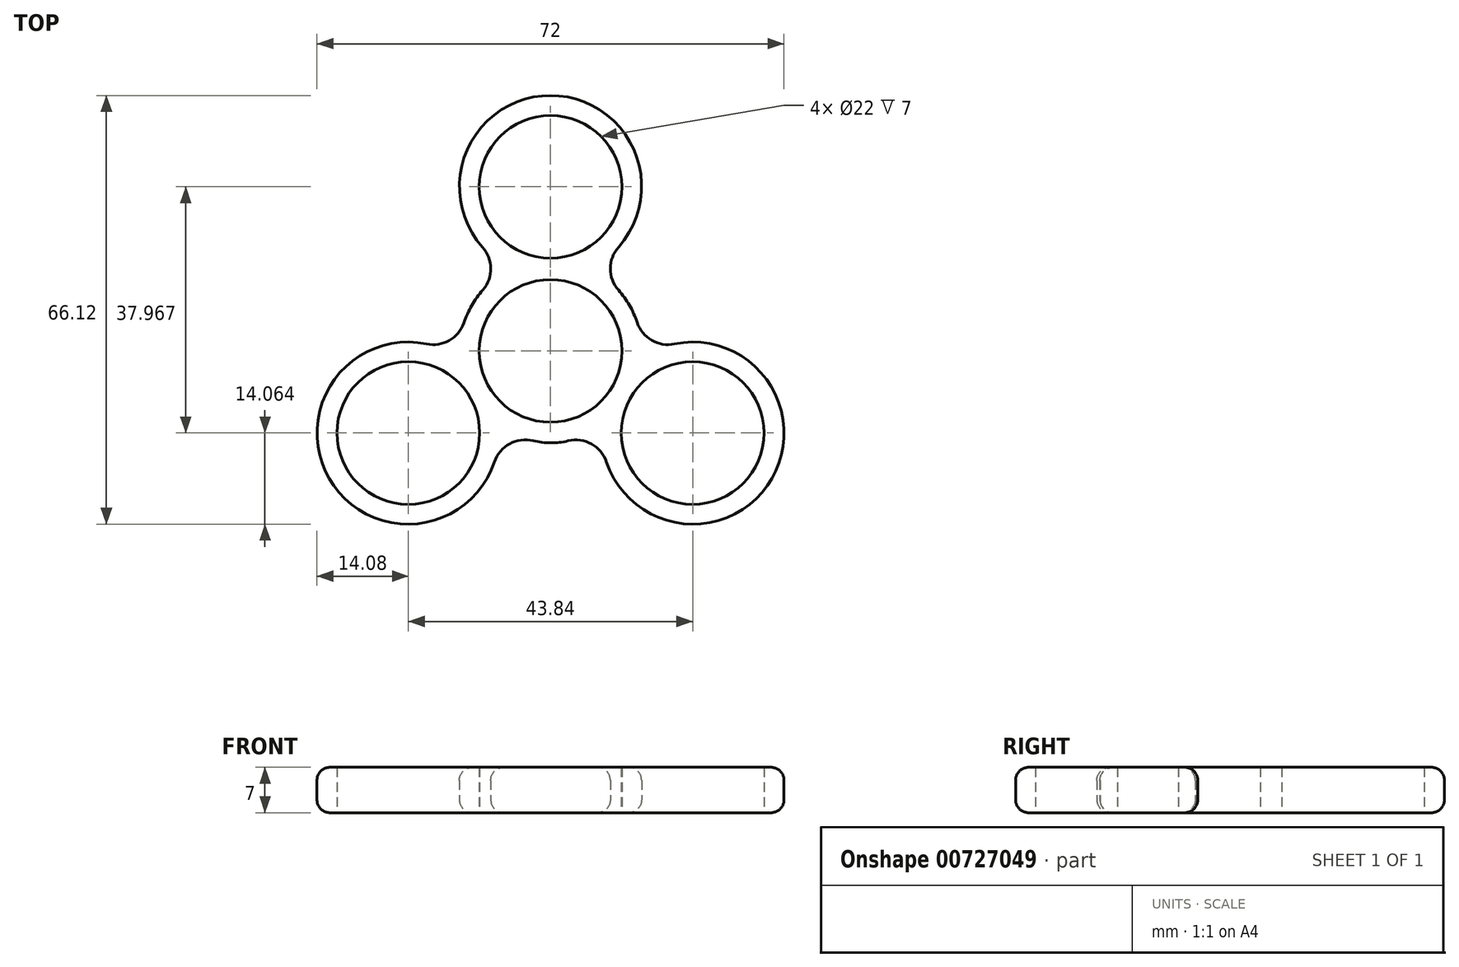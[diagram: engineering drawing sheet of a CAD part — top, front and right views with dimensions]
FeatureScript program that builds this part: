
annotation { "Feature Type Name" : "Feature", "Feature Type Description" : "" }
export const myFeature = defineFeature(function(context is Context, id is Id, definition is map)
    precondition{}
    {
        {
            var Q0;
            Q0=qCreatedBy(makeId("Top.planeOp"),FACE);
            var sketch = newSketch(context, id + "F0", { "sketchPlane" : qUnion([Q0])});
            skCircle(sketch, "E0", {"center": v(0, 0) * mm, "radius": 11 * mm});
            skCircle(sketch, "E1", {"center": v(0, 25.31) * mm, "radius": 11 * mm});
            skArc(sketch, "E2", {"start": v(10.49, 16.02) * mm, "mid": v(0, 39.4) * mm, "end": v(-10.48, 16.01) * mm});
            skArc(sketch, "E3.1.2", {"start": v(-19.1, 1.07) * mm, "mid": v(-34.13, -19.68) * mm, "end": v(-8.64, -17.12) * mm});
            skCircle(sketch, "E3.1.4", {"center": v(-21.92, -12.66) * mm, "radius": 11 * mm});
            skArc(sketch, "E3.2.2", {"start": v(8.64, -17.14) * mm, "mid": v(34.13, -19.68) * mm, "end": v(19.12, 1.07) * mm});
            skCircle(sketch, "E3.2.4", {"center": v(21.92, -12.66) * mm, "radius": 11 * mm});
            skArc(sketch, "E4", {"start": v(-10.42, 9.43) * mm, "mid": v(-12.13, 7.01) * mm, "end": v(-13.36, 4.33) * mm});
            skArc(sketch, "E5", {"start": v(13.36, 4.4) * mm, "mid": v(12.18, 7.03) * mm, "end": v(10.49, 9.37) * mm});
            skArc(sketch, "E6", {"start": v(-2.69, -13.85) * mm, "mid": v(0.02, -14.19) * mm, "end": v(2.72, -13.87) * mm});
            skPoint(sketch, "E7.newPointB", {"position": v(-8.44, -16.5) * mm});
            skArc(sketch, "E7.filletArc", {"start": v(-2.69, -13.85) * mm, "mid": v(-6.3, -14.32) * mm, "end": v(-8.64, -17.12) * mm});
            skPoint(sketch, "E8.newPointB", {"position": v(8.35, -16.14) * mm});
            skArc(sketch, "E8.filletArc", {"start": v(8.64, -17.14) * mm, "mid": v(6.32, -14.35) * mm, "end": v(2.72, -13.87) * mm});
            skPoint(sketch, "E9.newPointA", {"position": v(18.5, 0.93) * mm});
            skArc(sketch, "E9.filletArc", {"start": v(13.36, 4.4) * mm, "mid": v(15.6, 1.64) * mm, "end": v(19.12, 1.07) * mm});
            skPoint(sketch, "E10.newPointB", {"position": v(9.8, 15.3) * mm});
            skArc(sketch, "E10.filletArc", {"start": v(10.49, 16.02) * mm, "mid": v(9.22, 12.7) * mm, "end": v(10.49, 9.37) * mm});
            skPoint(sketch, "E11.newPointA", {"position": v(-10.06, 15.56) * mm});
            skArc(sketch, "E11.filletArc", {"start": v(-10.42, 9.43) * mm, "mid": v(-9.22, 12.73) * mm, "end": v(-10.48, 16.01) * mm});
            skPoint(sketch, "E12.newPointB", {"position": v(-18.15, 0.84) * mm});
            skArc(sketch, "E12.filletArc", {"start": v(-19.1, 1.07) * mm, "mid": v(-15.62, 1.62) * mm, "end": v(-13.36, 4.33) * mm});
            skSolve(sketch);
        }
        {
            var Q0;
            Q0 = qSketchRegion(id + "F0", true);
            extrude(context, id + "F1", {"entities" : qUnion([Q0]), "depth" : 7 * mm, "offsetDistance" : 25 * mm});
        }
        {
            var Q0;
            Q0=makeQuery(id+"F1.opExtrude","CAP_EDGE",EDGE,{"disambiguationData":[OSD([sQuery(id+"F0.wireOp",EDGE,"E4")])],"isStart":false});
            var Q1;
            Q1=makeQuery(id+"F1.opExtrude","CAP_EDGE",EDGE,{"disambiguationData":[OSD([sQuery(id+"F0.wireOp",EDGE,"E11.filletArc")])],"isStart":false});
            var Q2;
            Q2=makeQuery(id+"F1.opExtrude","CAP_EDGE",EDGE,{"disambiguationData":[OSD([sQuery(id+"F0.wireOp",EDGE,"E2")])],"isStart":false});
            var Q3;
            Q3=makeQuery(id+"F1.opExtrude","CAP_EDGE",EDGE,{"disambiguationData":[OSD([sQuery(id+"F0.wireOp",EDGE,"E5")])],"isStart":false});
            var Q4;
            Q4=makeQuery(id+"F1.opExtrude","CAP_EDGE",EDGE,{"disambiguationData":[OSD([sQuery(id+"F0.wireOp",EDGE,"E9.filletArc")])],"isStart":false});
            var Q5;
            Q5=makeQuery(id+"F1.opExtrude","CAP_EDGE",EDGE,{"disambiguationData":[OSD([sQuery(id+"F0.wireOp",EDGE,"E3.2.2")])],"isStart":false});
            var Q6;
            Q6=makeQuery(id+"F1.opExtrude","CAP_EDGE",EDGE,{"disambiguationData":[OSD([sQuery(id+"F0.wireOp",EDGE,"E8.filletArc")])],"isStart":false});
            var Q7;
            Q7=makeQuery(id+"F1.opExtrude","CAP_EDGE",EDGE,{"disambiguationData":[OSD([sQuery(id+"F0.wireOp",EDGE,"E6")])],"isStart":false});
            var Q8;
            Q8=makeQuery(id+"F1.opExtrude","CAP_EDGE",EDGE,{"disambiguationData":[OSD([sQuery(id+"F0.wireOp",EDGE,"E7.filletArc")])],"isStart":false});
            var Q9;
            Q9=makeQuery(id+"F1.opExtrude","CAP_EDGE",EDGE,{"disambiguationData":[OSD([sQuery(id+"F0.wireOp",EDGE,"E3.1.2")])],"isStart":false});
            var Q10;
            Q10=makeQuery(id+"F1.opExtrude","CAP_EDGE",EDGE,{"disambiguationData":[OSD([sQuery(id+"F0.wireOp",EDGE,"E12.filletArc")])],"isStart":false});
            var Q11;
            Q11=makeQuery(id+"F1.opExtrude","CAP_EDGE",EDGE,{"disambiguationData":[OSD([sQuery(id+"F0.wireOp",EDGE,"E5")])],"isStart":true});
            var Q12;
            Q12=makeQuery(id+"F1.opExtrude","CAP_EDGE",EDGE,{"disambiguationData":[OSD([sQuery(id+"F0.wireOp",EDGE,"E9.filletArc")])],"isStart":true});
            var Q13;
            Q13=makeQuery(id+"F1.opExtrude","CAP_EDGE",EDGE,{"disambiguationData":[OSD([sQuery(id+"F0.wireOp",EDGE,"E6")])],"isStart":true});
            var Q14;
            Q14=makeQuery(id+"F1.opExtrude","CAP_EDGE",EDGE,{"disambiguationData":[OSD([sQuery(id+"F0.wireOp",EDGE,"E8.filletArc")])],"isStart":true});
            var Q15;
            Q15=makeQuery(id+"F1.opExtrude","CAP_EDGE",EDGE,{"disambiguationData":[OSD([sQuery(id+"F0.wireOp",EDGE,"E7.filletArc")])],"isStart":true});
            var Q16;
            Q16=makeQuery(id+"F1.opExtrude","CAP_EDGE",EDGE,{"disambiguationData":[OSD([sQuery(id+"F0.wireOp",EDGE,"E3.1.2")])],"isStart":true});
            var Q17;
            Q17=makeQuery(id+"F1.opExtrude","CAP_EDGE",EDGE,{"disambiguationData":[OSD([sQuery(id+"F0.wireOp",EDGE,"E12.filletArc")])],"isStart":true});
            var Q18;
            Q18=makeQuery(id+"F1.opExtrude","CAP_EDGE",EDGE,{"disambiguationData":[OSD([sQuery(id+"F0.wireOp",EDGE,"E4")])],"isStart":true});
            var Q19;
            Q19=makeQuery(id+"F1.opExtrude","CAP_EDGE",EDGE,{"disambiguationData":[OSD([sQuery(id+"F0.wireOp",EDGE,"E11.filletArc")])],"isStart":true});
            var Q20;
            Q20=makeQuery(id+"F1.opExtrude","CAP_EDGE",EDGE,{"disambiguationData":[OSD([sQuery(id+"F0.wireOp",EDGE,"E2")])],"isStart":true});
            var Q21;
            Q21=makeQuery(id+"F1.opExtrude","CAP_EDGE",EDGE,{"disambiguationData":[OSD([sQuery(id+"F0.wireOp",EDGE,"E10.filletArc")])],"isStart":true});
            var Q22;
            Q22=makeQuery(id+"F1.opExtrude","CAP_EDGE",EDGE,{"disambiguationData":[OSD([sQuery(id+"F0.wireOp",EDGE,"E3.2.2")])],"isStart":true});
            fillet(context, id + "F2", {"entities" : qUnion([Q0, Q1, Q2, Q3, Q4, Q5, Q6, Q7, Q8, Q9, Q10, Q11, Q12, Q13, Q14, Q15, Q16, Q17, Q18, Q19, Q20, Q21, Q22]), "radius" : 2 * mm, "tangentPropagation" : true, "allowEdgeOverflow" : false});
        }
    });
